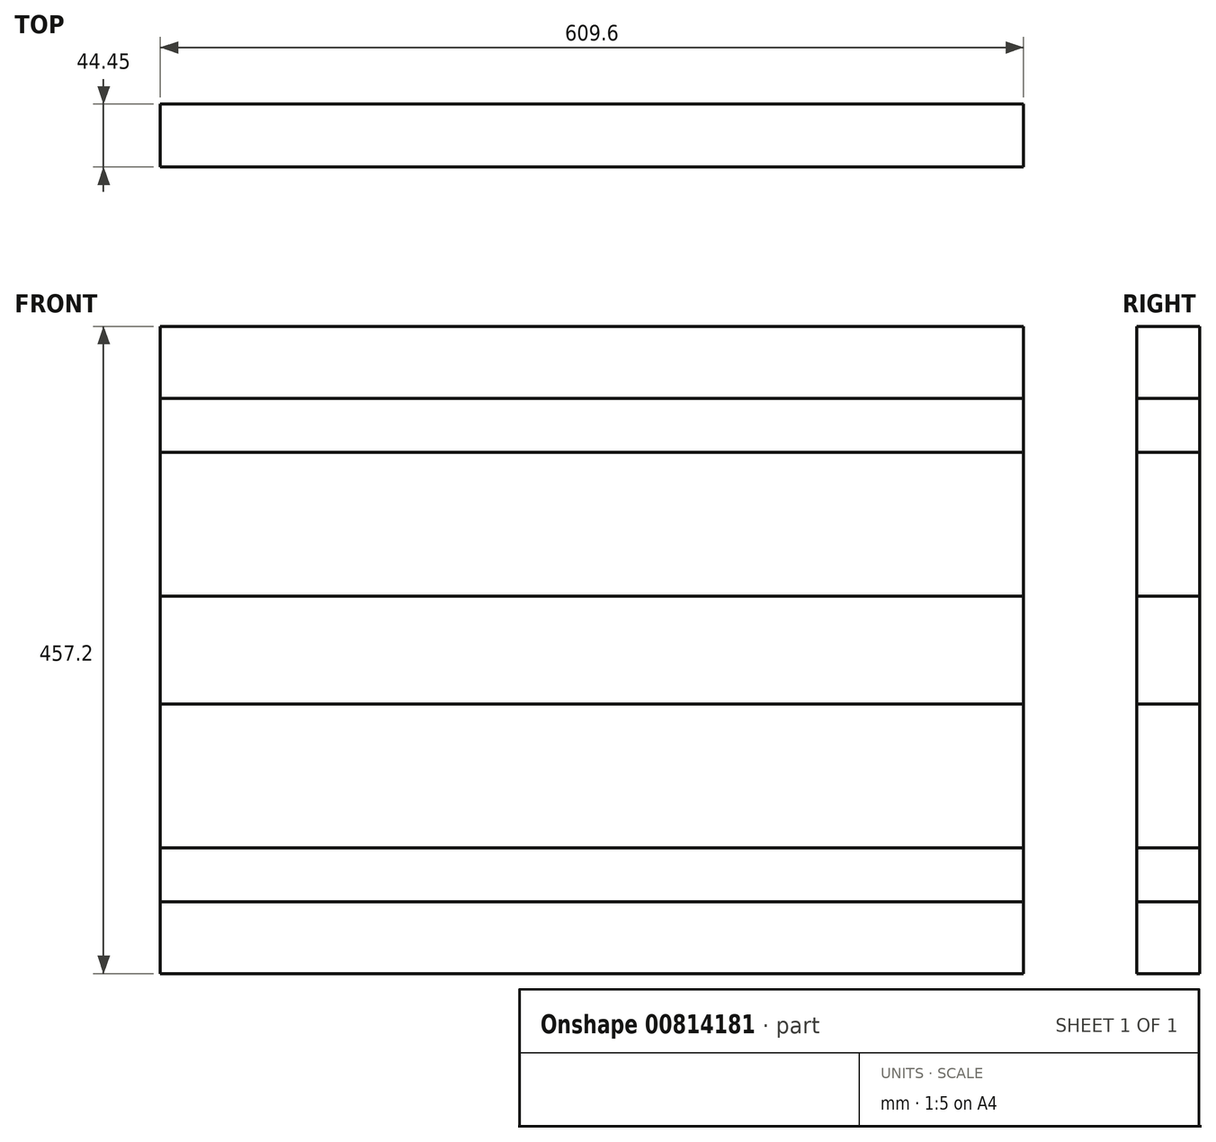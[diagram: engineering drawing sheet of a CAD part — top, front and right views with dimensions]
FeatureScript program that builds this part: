
annotation { "Feature Type Name" : "Feature", "Feature Type Description" : "" }
export const myFeature = defineFeature(function(context is Context, id is Id, definition is map)
    precondition{}
    {
        {
            var Q0;
            Q0=qCreatedBy(makeId("Front.planeOp"),FACE);
            var sketch = newSketch(context, id + "F0", { "sketchPlane" : qUnion([Q0])});
            skLineSegment(sketch, "E0.bottom", {"start": v(-158.98, 190.5) * mm, "end": v(450.62, 190.5) * mm});
            skLineSegment(sketch, "E0.top", {"start": v(-158.98, -266.7) * mm, "end": v(450.62, -266.7) * mm});
            skLineSegment(sketch, "E0.left", {"start": v(-158.98, 190.5) * mm, "end": v(-158.98, -266.7) * mm});
            skLineSegment(sketch, "E0.right", {"start": v(450.62, 190.5) * mm, "end": v(450.62, -266.7) * mm});
            skLineSegment(sketch, "E1.bottom", {"start": v(-158.98, 139.7) * mm, "end": v(450.62, 139.7) * mm});
            skLineSegment(sketch, "E1.top", {"start": v(-158.98, 101.6) * mm, "end": v(450.62, 101.6) * mm});
            skLineSegment(sketch, "E1.left", {"start": v(-158.98, 139.7) * mm, "end": v(-158.98, 101.6) * mm});
            skLineSegment(sketch, "E1.right", {"start": v(450.62, 139.7) * mm, "end": v(450.62, 101.6) * mm});
            skLineSegment(sketch, "E2.bottom", {"start": v(-158.98, -177.8) * mm, "end": v(450.62, -177.8) * mm});
            skLineSegment(sketch, "E2.top", {"start": v(-158.98, -215.9) * mm, "end": v(450.62, -215.9) * mm});
            skLineSegment(sketch, "E2.left", {"start": v(-158.98, -177.8) * mm, "end": v(-158.98, -215.9) * mm});
            skLineSegment(sketch, "E2.right", {"start": v(450.62, -177.8) * mm, "end": v(450.62, -215.9) * mm});
            skLineSegment(sketch, "E3.bottom", {"start": v(-158.98, 0) * mm, "end": v(450.62, 0) * mm});
            skLineSegment(sketch, "E3.top", {"start": v(-158.98, -76.2) * mm, "end": v(450.62, -76.2) * mm});
            skLineSegment(sketch, "E3.left", {"start": v(-158.98, 0) * mm, "end": v(-158.98, -76.2) * mm});
            skLineSegment(sketch, "E3.right", {"start": v(450.62, 0) * mm, "end": v(450.62, -76.2) * mm});
            skSolve(sketch);
        }
        {
            var Q0;
            Q0=makeQuery(id+"F0.imprint","IMPRINT",FACE,{"disambiguationData":[TD([[makeQuery(id+"F0.imprint","IMPRINT",EDGE,{"derivedFrom":sQuery(id+"F0.wireOp",EDGE,"E1.bottom")}),-1.0]])]});
            extrude(context, id + "F1", {"entities" : qUnion([Q0]), "depth" : 44.45 * mm, "offsetDistance" : 25.4 * mm});
        }
        {
            var Q0;
            Q0=makeQuery(id+"F0.imprint","IMPRINT",FACE,{"disambiguationData":[TD([[makeQuery(id+"F0.imprint","IMPRINT",EDGE,{"derivedFrom":sQuery(id+"F0.wireOp",EDGE,"E2.bottom")}),-1.0]])]});
            extrude(context, id + "F2", {"entities" : qUnion([Q0]), "depth" : 44.45 * mm, "offsetDistance" : 25.4 * mm});
        }
        {
            var Q0;
            {var subQ0=sQuery(id+"F0.wireOp",EDGE,"E1.top");Q0=makeQuery(id+"F0.imprint","IMPRINT",FACE,{"disambiguationData":[TD([[makeQuery(id+"F0.imprint","IMPRINT",EDGE,{"derivedFrom":subQ0}),-1.0]])]});}
            var Q1;
            {var subQ0=sQuery(id+"F0.wireOp",EDGE,"E0.bottom");Q1=makeQuery(id+"F0.imprint","IMPRINT",FACE,{"disambiguationData":[TD([[makeQuery(id+"F0.imprint","IMPRINT",EDGE,{"derivedFrom":subQ0}),-1.0]])]});}
            var Q2;
            {var subQ0=sQuery(id+"F0.wireOp",EDGE,"E0.top");Q2=makeQuery(id+"F0.imprint","IMPRINT",FACE,{"disambiguationData":[TD([[makeQuery(id+"F0.imprint","IMPRINT",EDGE,{"derivedFrom":subQ0}),1.0]])]});}
            extrude(context, id + "F3", {"entities" : qUnion([Q0, Q1, Q2]), "depth" : 44.45 * mm, "offsetDistance" : 25.4 * mm});
        }
        {
            var Q0;
            Q0=makeQuery(id+"F0.imprint","IMPRINT",FACE,{"disambiguationData":[TD([[makeQuery(id+"F0.imprint","IMPRINT",EDGE,{"derivedFrom":sQuery(id+"F0.wireOp",EDGE,"E3.bottom")}),-1.0]])]});
            extrude(context, id + "F4", {"entities" : qUnion([Q0]), "depth" : 44.45 * mm, "offsetDistance" : 25.4 * mm});
        }
        {
            var Q0;
            {var subQ0=sQuery(id+"F0.wireOp",EDGE,"E2.bottom");Q0=makeQuery(id+"F0.imprint","IMPRINT",FACE,{"disambiguationData":[TD([[makeQuery(id+"F0.imprint","IMPRINT",EDGE,{"derivedFrom":subQ0}),1.0]])]});}
            extrude(context, id + "F5", {"entities" : qUnion([Q0]), "depth" : 44.45 * mm, "offsetDistance" : 25.4 * mm});
        }
    });
